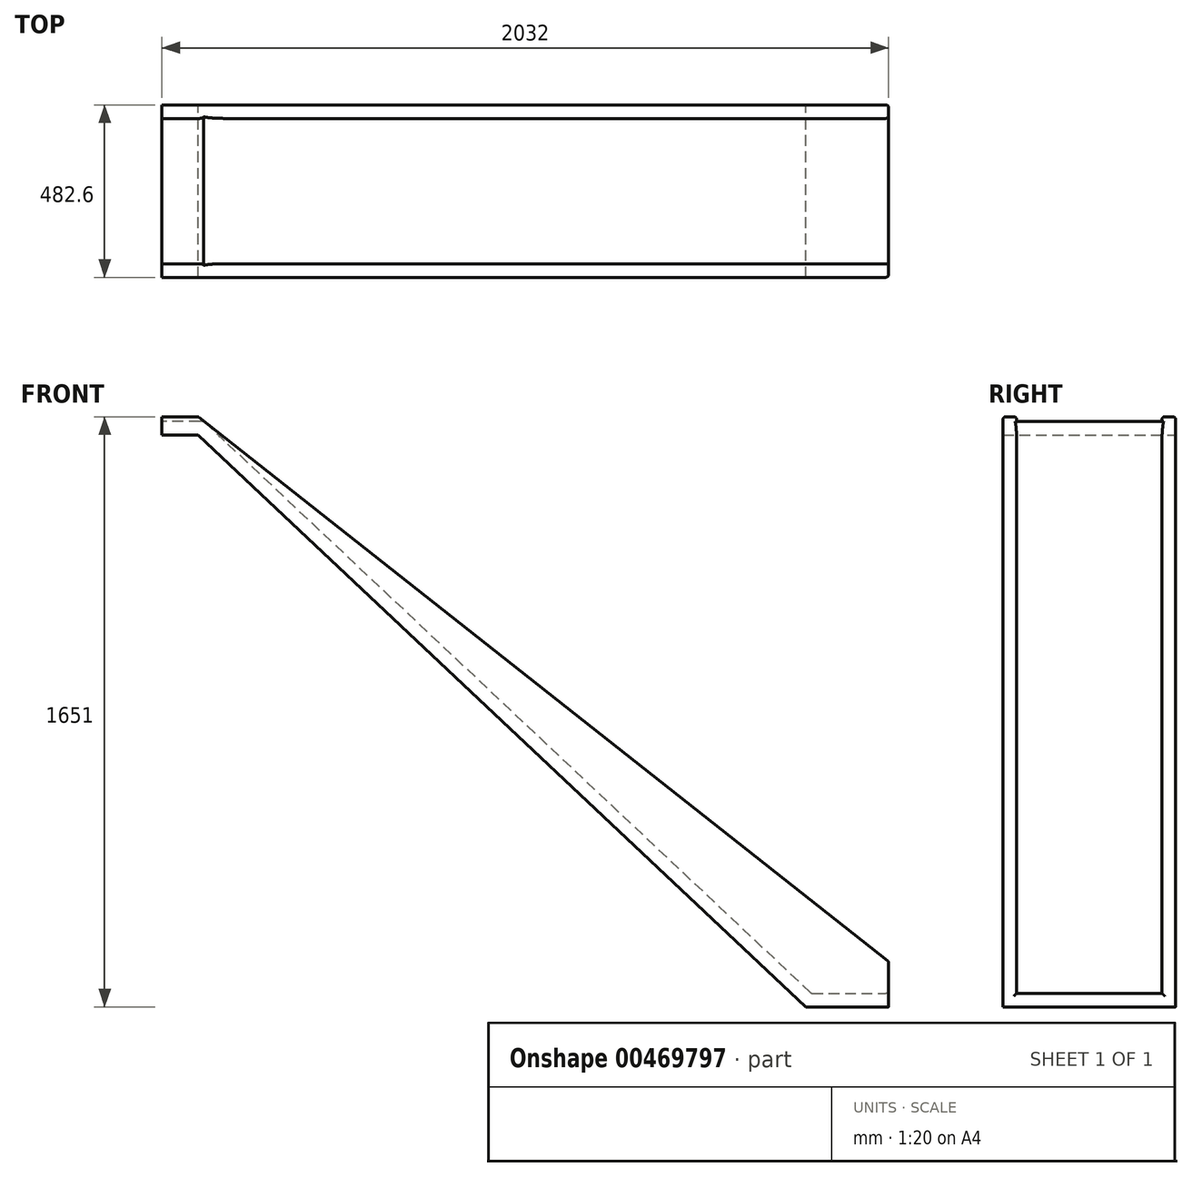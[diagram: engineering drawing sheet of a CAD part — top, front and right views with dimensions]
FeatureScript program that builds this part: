
annotation { "Feature Type Name" : "Feature", "Feature Type Description" : "" }
export const myFeature = defineFeature(function(context is Context, id is Id, definition is map)
    precondition{}
    {
        {
            var Q0;
            Q0=qCreatedBy(makeId("Front.planeOp"),FACE);
            var sketch = newSketch(context, id + "F0", { "sketchPlane" : qUnion([Q0])});
            skLineSegment(sketch, "E0", {"start": v(0, 0) * mm, "end": v(231.72, 0) * mm});
            skLineSegment(sketch, "E1", {"start": v(231.72, 0) * mm, "end": v(231.72, 127) * mm});
            skLineSegment(sketch, "E2", {"start": v(0, 0) * mm, "end": v(-1698.68, 1600.2) * mm});
            skLineSegment(sketch, "E3", {"start": v(-1698.68, 1600.2) * mm, "end": v(-1800.28, 1600.2) * mm});
            skLineSegment(sketch, "E4", {"start": v(-1800.28, 1600.2) * mm, "end": v(-1800.28, 1651) * mm});
            skLineSegment(sketch, "E5", {"start": v(-1800.28, 1651) * mm, "end": v(-1698.68, 1651) * mm});
            skLineSegment(sketch, "E6", {"start": v(-1698.68, 1651) * mm, "end": v(231.72, 127) * mm});
            skSolve(sketch);
        }
        {
            var Q0;
            Q0=qSketchRegion(id+"F0",true);
            extrude(context, id + "F1", {"entities" : qUnion([Q0]), "depth" : 482.6 * mm});
        }
        {
            var Q0;
            Q0=makeQuery(id+"F1.opExtrude","SWEPT_FACE",FACE,{"disambiguationData":[OSD([sQuery(id+"F0.wireOp",EDGE,"E6")])]});
            var Q1;
            Q1=makeQuery(id+"F1.opExtrude","SWEPT_FACE",FACE,{"disambiguationData":[OSD([sQuery(id+"F0.wireOp",EDGE,"E1")])]});
            var Q2;
            Q2=makeQuery(id+"F1.opExtrude","SWEPT_FACE",FACE,{"disambiguationData":[OSD([sQuery(id+"F0.wireOp",EDGE,"E5")])]});
            var Q3;
            Q3=makeQuery(id+"F1.opExtrude","SWEPT_FACE",FACE,{"disambiguationData":[OSD([sQuery(id+"F0.wireOp",EDGE,"E4")])]});
            shell(context, id + "F2", {"entities" : qUnion([Q0, Q1, Q2, Q3]), "thickness" : 38.1 * mm});
        }
        {
            var Q0;
            {var subQ0=sQuery(id+"F0.wireOp",EDGE,"E5");Q0=makeQuery(id+"F2.opShell","OFFSET_EDGE",EDGE,{"disambiguationData":[OSD([subQ0]),TDD([makeQuery(id+"F1.opExtrude","CAP_EDGE",EDGE,{"disambiguationData":[OSD([subQ0])],"isStart":false})])]});}
            var Q1;
            {var subQ0=sQuery(id+"F0.wireOp",EDGE,"E6");Q1=makeQuery(id+"F2.opShell","OFFSET_EDGE",EDGE,{"disambiguationData":[OSD([subQ0]),TDD([makeQuery(id+"F1.opExtrude","CAP_EDGE",EDGE,{"disambiguationData":[OSD([subQ0])],"isStart":false})])]});}
            var Q2;
            Q2=makeQuery(id+"F1.opExtrude","CAP_EDGE",EDGE,{"disambiguationData":[OSD([sQuery(id+"F0.wireOp",EDGE,"E5")])],"isStart":false});
            var Q3;
            Q3=makeQuery(id+"F1.opExtrude","CAP_EDGE",EDGE,{"disambiguationData":[OSD([sQuery(id+"F0.wireOp",EDGE,"E6")])],"isStart":false});
            var Q4;
            {var subQ0=sQuery(id+"F0.wireOp",EDGE,"E5");Q4=makeQuery(id+"F2.opShell","OFFSET_EDGE",EDGE,{"disambiguationData":[OSD([subQ0]),TDD([makeQuery(id+"F1.opExtrude","CAP_EDGE",EDGE,{"disambiguationData":[OSD([subQ0])],"isStart":true})])]});}
            var Q5;
            Q5=makeQuery(id+"F1.opExtrude","CAP_EDGE",EDGE,{"disambiguationData":[OSD([sQuery(id+"F0.wireOp",EDGE,"E5")])],"isStart":true});
            var Q6;
            Q6=makeQuery(id+"F1.opExtrude","CAP_EDGE",EDGE,{"disambiguationData":[OSD([sQuery(id+"F0.wireOp",EDGE,"E6")])],"isStart":true});
            var Q7;
            {var subQ0=sQuery(id+"F0.wireOp",EDGE,"E6");Q7=makeQuery(id+"F2.opShell","OFFSET_EDGE",EDGE,{"disambiguationData":[OSD([subQ0]),TDD([makeQuery(id+"F1.opExtrude","CAP_EDGE",EDGE,{"disambiguationData":[OSD([subQ0])],"isStart":true})])]});}
            var Q8;
            Q8=makeQuery(id+"F2.opShell","OFFSET_EDGE",EDGE,{"disambiguationData":[OSD([sQuery(id+"F0.wireOp",EDGE,"E5"),sQuery(id+"F0.wireOp",EDGE,"E6")])]});
            var Q9;
            Q9=makeQuery(id+"F1.opExtrude","SWEPT_EDGE",EDGE,{"disambiguationData":[OSD([sQuery(id+"F0.wireOp",EDGE,"E5"),sQuery(id+"F0.wireOp",EDGE,"E6")])]});
            var Q10;
            Q10=makeQuery(id+"F1.opExtrude","SWEPT_EDGE",EDGE,{"disambiguationData":[OSD([sQuery(id+"F0.wireOp",EDGE,"E1"),sQuery(id+"F0.wireOp",EDGE,"E6")])]});
            var Q11;
            Q11=makeQuery(id+"F1.opExtrude","CAP_EDGE",EDGE,{"disambiguationData":[OSD([sQuery(id+"F0.wireOp",EDGE,"E1")])],"isStart":false});
            var Q12;
            Q12=makeQuery(id+"F2.opShell","OFFSET_EDGE",EDGE,{"disambiguationData":[OSD([sQuery(id+"F0.wireOp",EDGE,"E1"),sQuery(id+"F0.wireOp",EDGE,"E6")])]});
            var Q13;
            Q13=makeQuery(id+"F1.opExtrude","CAP_EDGE",EDGE,{"disambiguationData":[OSD([sQuery(id+"F0.wireOp",EDGE,"E1")])],"isStart":true});
            var Q14;
            {var subQ0=sQuery(id+"F0.wireOp",EDGE,"E1");Q14=makeQuery(id+"F2.opShell","OFFSET_EDGE",EDGE,{"disambiguationData":[OSD([subQ0]),TDD([makeQuery(id+"F1.opExtrude","CAP_EDGE",EDGE,{"disambiguationData":[OSD([subQ0])],"isStart":true})])]});}
            var Q15;
            {var subQ0=sQuery(id+"F0.wireOp",EDGE,"E1");Q15=makeQuery(id+"F2.opShell","OFFSET_EDGE",EDGE,{"disambiguationData":[OSD([subQ0]),TDD([makeQuery(id+"F1.opExtrude","CAP_EDGE",EDGE,{"disambiguationData":[OSD([subQ0])],"isStart":false})])]});}
            var Q16;
            Q16=makeQuery(id+"F2.opShell","OFFSET_EDGE",EDGE,{"disambiguationData":[OSD([sQuery(id+"F0.wireOp",EDGE,"E0"),sQuery(id+"F0.wireOp",EDGE,"E1")])]});
            var Q17;
            Q17=makeQuery(id+"F2.opShell","OFFSET_EDGE",EDGE,{"disambiguationData":[OSD([sQuery(id+"F0.wireOp",EDGE,"E0"),sQuery(id+"F0.wireOp",EDGE,"E2")])]});
            fillet(context, id + "F3", {"entities" : qUnion([Q0, Q1, Q2, Q3, Q4, Q5, Q6, Q7, Q8, Q9, Q10, Q11, Q12, Q13, Q14, Q15, Q16, Q17]), "radius" : 7.62 * mm, "tangentPropagation" : true, "allowEdgeOverflow" : false});
        }
    });
